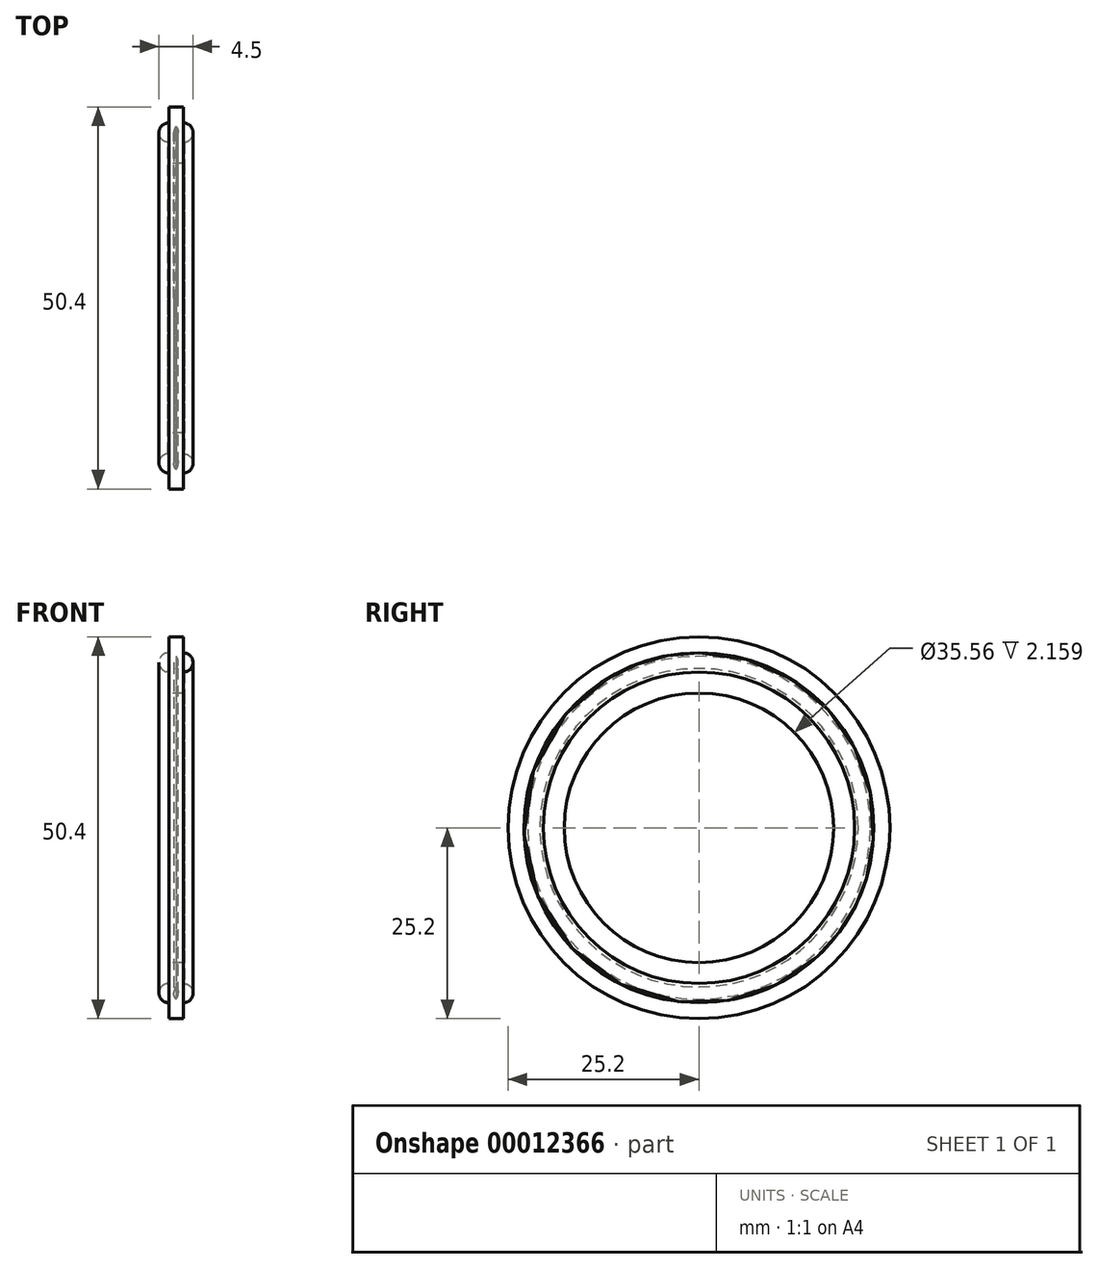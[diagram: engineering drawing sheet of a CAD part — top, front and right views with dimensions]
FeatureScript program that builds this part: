
annotation { "Feature Type Name" : "Feature", "Feature Type Description" : "" }
export const myFeature = defineFeature(function(context is Context, id is Id, definition is map)
    precondition{}
    {
        {
            var Q0;
            Q0=qCreatedBy(makeId("Top.planeOp"),FACE);
            var sketch = newSketch(context, id + "F0", { "sketchPlane" : qUnion([Q0])});
            skCircle(sketch, "E0", {"center": v(-0.98, 21.82) * mm, "radius": 1.27 * mm});
            skLineSegment(sketch, "E1", {"start": v(-0.95, 23.09) * mm, "end": v(-0.95, 25.2) * mm});
            skLineSegment(sketch, "E2", {"start": v(-1.08, 20.55) * mm, "end": v(-1.08, 17.78) * mm});
            skLineSegment(sketch, "E3.0.MirrorCS", {"start": v(0.95, 23.09) * mm, "end": v(0.95, 25.2) * mm});
            skCircle(sketch, "E4.0.MirrorC", {"center": v(0.98, 21.82) * mm, "radius": 1.27 * mm});
            skLineSegment(sketch, "E5.0.MirrorCS", {"start": v(1.08, 20.55) * mm, "end": v(1.08, 17.78) * mm});
            skLineSegment(sketch, "E6", {"start": v(-0.95, 25.2) * mm, "end": v(0.95, 25.2) * mm});
            skLineSegment(sketch, "E7", {"start": v(-1.08, 17.78) * mm, "end": v(1.08, 17.78) * mm});
            skLineSegment(sketch, "E8.0.MirrorCS", {"start": v(-0.95, -25.2) * mm, "end": v(0.95, -25.2) * mm});
            skLineSegment(sketch, "E8.1.MirrorCS", {"start": v(-1.08, -17.78) * mm, "end": v(1.08, -17.78) * mm});
            skCircle(sketch, "E8.2.MirrorC", {"center": v(-0.98, -21.82) * mm, "radius": 1.27 * mm});
            skCircle(sketch, "E8.3.MirrorC", {"center": v(0.98, -21.82) * mm, "radius": 1.27 * mm});
            skLineSegment(sketch, "E8.4.MirrorCS", {"start": v(0.95, -23.09) * mm, "end": v(0.95, -25.2) * mm});
            skLineSegment(sketch, "E8.5.MirrorCS", {"start": v(-0.95, -23.09) * mm, "end": v(-0.95, -25.2) * mm});
            skLineSegment(sketch, "E8.6.MirrorCS", {"start": v(-1.08, -20.55) * mm, "end": v(-1.08, -17.78) * mm});
            skLineSegment(sketch, "E8.7.MirrorCS", {"start": v(1.08, -20.55) * mm, "end": v(1.08, -17.78) * mm});
            skLineSegment(sketch, "E9", {"start": v(-18.77, 0) * mm, "end": v(15.8, 0) * mm, "construction": true});
            skSolve(sketch);
        }
        {
            var Q0;
            {var subQ4=sQuery(id+"F0.wireOp",EDGE,"E2");Q0=makeQuery(id+"F0.imprint","IMPRINT",FACE,{"disambiguationData":[TD([[makeQuery(id+"F0.imprint","IMPRINT",EDGE,{"derivedFrom":subQ4}),1.0]])]});}
            var Q1;
            {var subQ1=sQuery(id+"F0.wireOp",EDGE,"E0");var subQ5=makeQuery(id+"F0.imprint","INTERSECT",VERTEX,{"derivedFrom":[subQ1,sQuery(id+"F0.wireOp",EDGE,"E1")]});Q1=makeQuery(id+"F0.imprint","IMPRINT",FACE,{"disambiguationData":[TD([[makeQuery(id+"F0.imprint","IMPRINT",EDGE,{"disambiguationData":[TD([[subQ5,1.0]])],"derivedFrom":subQ1}),1.0]])]});}
            var Q2;
            {var subQ1=sQuery(id+"F0.wireOp",EDGE,"E1");Q2=makeQuery(id+"F0.imprint","IMPRINT",FACE,{"disambiguationData":[TD([[makeQuery(id+"F0.imprint","IMPRINT",EDGE,{"derivedFrom":subQ1}),-1.0]])]});}
            var Q3;
            {var subQ0=sQuery(id+"F0.wireOp",EDGE,"E4.0.MirrorC");var subQ1=sQuery(id+"F0.wireOp",EDGE,"E0");var subQ5=makeQuery(id+"F0.imprint","INTERSECT",VERTEX,{"disambiguationData":[OD(0.0)],"derivedFrom":[subQ1,subQ0]});Q3=makeQuery(id+"F0.imprint","IMPRINT",FACE,{"disambiguationData":[TD([[makeQuery(id+"F0.imprint","IMPRINT",EDGE,{"disambiguationData":[TD([[subQ5,1.0]])],"derivedFrom":subQ1}),-1.0]])]});}
            var Q4;
            Q4=sQuery(id+"F0.wireOp",EDGE,"E9");
            revolve(context, id + "F1", {"entities" : qUnion([Q0, Q1, Q2, Q3]), "axis" : qUnion([Q4]), "revolveType" : RevolveType.FULL});
        }
    });
